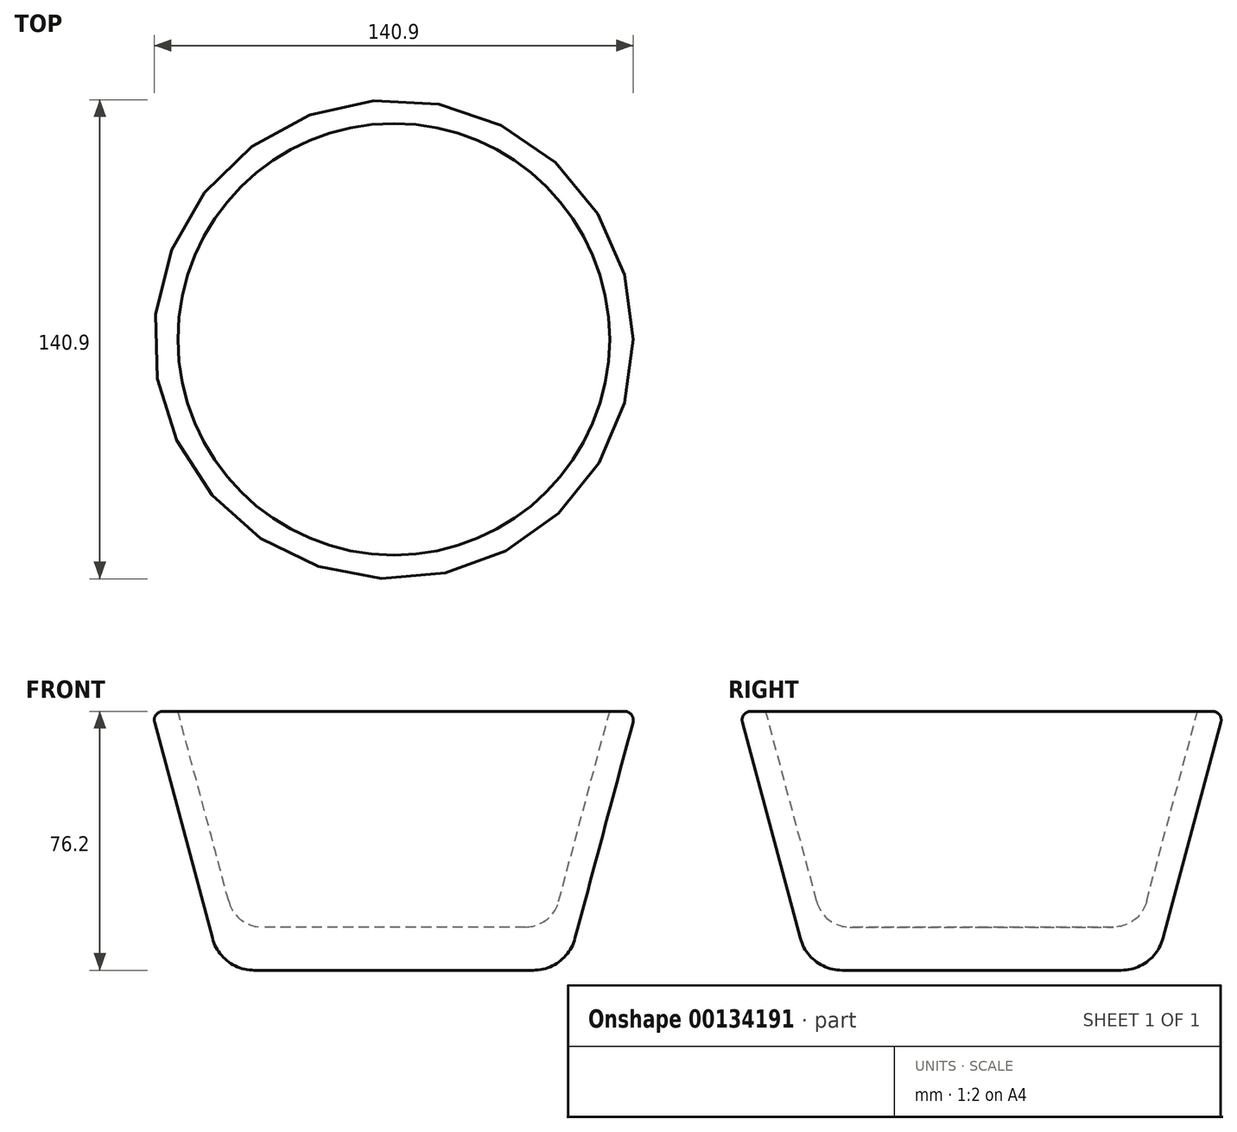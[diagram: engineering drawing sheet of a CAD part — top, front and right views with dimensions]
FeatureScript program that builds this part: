
annotation { "Feature Type Name" : "Feature", "Feature Type Description" : "" }
export const myFeature = defineFeature(function(context is Context, id is Id, definition is map)
    precondition{}
    {
        {
            var Q0;
            Q0=qCreatedBy(makeId("Top.planeOp"),FACE);
            var sketch = newSketch(context, id + "F0", { "sketchPlane" : qUnion([Q0])});
            skCircle(sketch, "E0", {"center": v(0, 0) * mm, "radius": 50.8 * mm});
            skCircle(sketch, "E1", {"center": v(-197.5, 43.52) * mm, "radius": 35.7 * mm});
            skSolve(sketch);
        }
        {
            var Q0;
            Q0=makeQuery(id+"F0.imprint","IMPRINT",FACE,{"disambiguationData":[TD([[makeQuery(id+"F0.imprint","IMPRINT",EDGE,{"derivedFrom":sQuery(id+"F0.wireOp",EDGE,"E0")}),1.0]])]});
            extrude(context, id + "F1", {"entities" : qUnion([Q0]), "depth" : 76.2 * mm, "hasDraft" : true, "draftAngle" : 15 * degree});
        }
        {
            var Q0;
            Q0=makeQuery(id+"F1.opExtrude","CAP_FACE",FACE,{"disambiguationData":[OSD([sQuery(id+"F0.wireOp",EDGE,"E0")])],"isStart":false});
            var sketch = newSketch(context, id + "F2", { "sketchPlane" : qUnion([Q0])});
            skCircle(sketch, "E2", {"center": v(0, 0) * mm, "radius": 63.5 * mm});
            skSolve(sketch);
        }
        {
            var Q0;
            Q0 = qSketchRegion(id + "F2", true);
            extrude(context, id + "F3", {"entities" : qUnion([Q0]), "operationType" : NewBodyOperationType.REMOVE, "oppositeDirection" : true, "depth" : 63.5 * mm, "hasDraft" : true, "draftAngle" : 15 * degree, "draftPullDirection" : true});
        }
        {
            var Q0;
            Q0=makeQuery(id+"F1.opExtrude","CAP_EDGE",EDGE,{"disambiguationData":[OSD([sQuery(id+"F0.wireOp",EDGE,"E0")])],"isStart":false});
            var Q1;
            Q1=makeQuery(id+"F3.boolean.opBoolean","COPY",EDGE,{"derivedFrom":makeQuery(id+"F3.opExtrude","CAP_EDGE",EDGE,{"disambiguationData":[OSD([sQuery(id+"F2.wireOp",EDGE,"E2")])],"isStart":true})});
            fillet(context, id + "F4", {"entities" : qUnion([Q0, Q1]), "radius" : 2.54 * mm, "tangentPropagation" : true, "allowEdgeOverflow" : false});
        }
        {
            var Q0;
            Q0=makeQuery(id+"F1.opExtrude","CAP_EDGE",EDGE,{"disambiguationData":[OSD([sQuery(id+"F0.wireOp",EDGE,"E0")])],"isStart":true});
            fillet(context, id + "F5", {"entities" : qUnion([Q0]), "radius" : 12.7 * mm, "tangentPropagation" : true, "allowEdgeOverflow" : false});
        }
        {
            var Q0;
            Q0=makeQuery(id+"F3.boolean.opBoolean","COPY",EDGE,{"derivedFrom":makeQuery(id+"F3.opExtrude","CAP_EDGE",EDGE,{"disambiguationData":[OSD([sQuery(id+"F2.wireOp",EDGE,"E2")])],"isStart":false})});
            fillet(context, id + "F6", {"entities" : qUnion([Q0]), "radius" : 10.16 * mm, "tangentPropagation" : true, "allowEdgeOverflow" : false});
        }
    });
